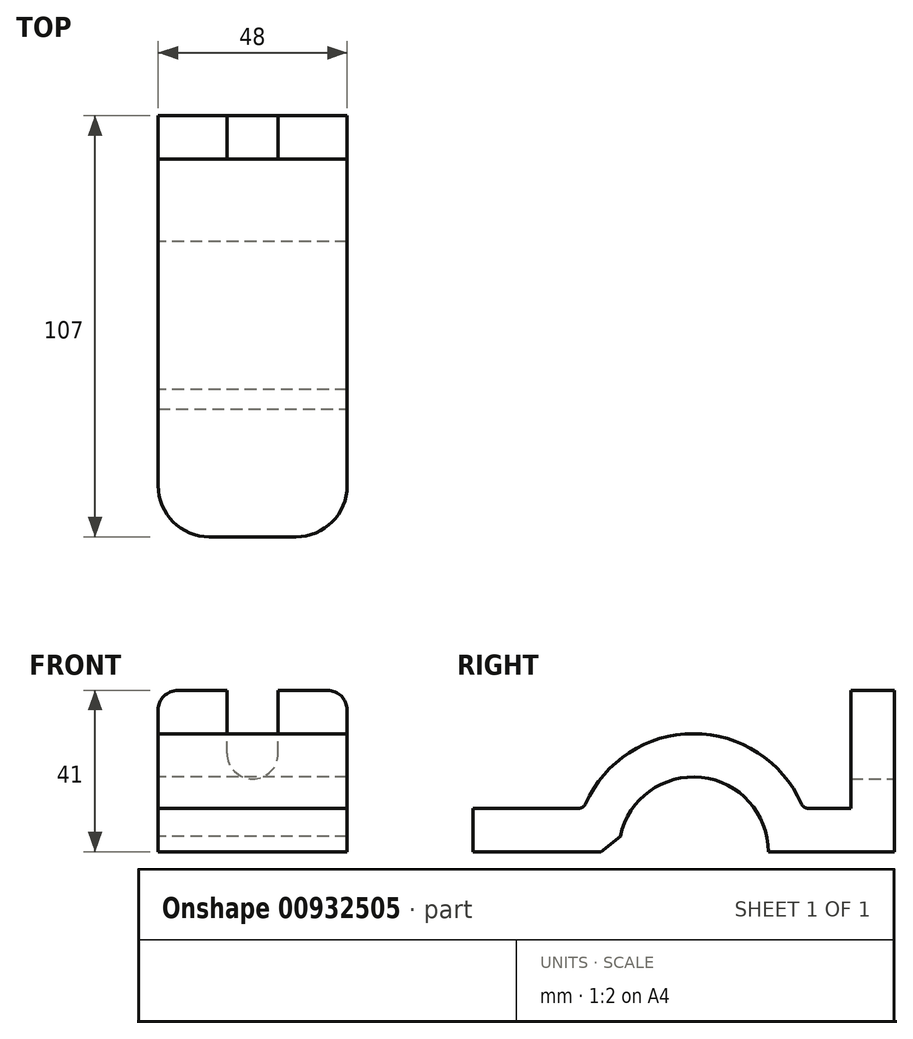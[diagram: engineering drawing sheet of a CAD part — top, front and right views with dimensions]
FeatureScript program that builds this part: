
annotation { "Feature Type Name" : "Feature", "Feature Type Description" : "" }
export const myFeature = defineFeature(function(context is Context, id is Id, definition is map)
    precondition{}
    {
        {
            var Q0;
            Q0=qCreatedBy(makeId("Right.planeOp"),FACE);
            var sketch = newSketch(context, id + "F0", { "sketchPlane" : qUnion([Q0])});
            skCircle(sketch, "E0", {"center": v(0, 0) * mm, "radius": 19 * mm});
            skCircle(sketch, "E1", {"center": v(0, 0) * mm, "radius": 30 * mm});
            skLineSegment(sketch, "E2.bottom", {"start": v(-56, 0) * mm, "end": v(51, 0) * mm});
            skLineSegment(sketch, "E2.top", {"start": v(-56, 11) * mm, "end": v(51, 11) * mm});
            skLineSegment(sketch, "E2.left", {"start": v(-56, 0) * mm, "end": v(-56, 11) * mm});
            skLineSegment(sketch, "E2.right", {"start": v(51, 0) * mm, "end": v(51, 11) * mm});
            skLineSegment(sketch, "E3.bottom", {"start": v(51, 11) * mm, "end": v(40, 11) * mm});
            skLineSegment(sketch, "E3.top", {"start": v(51, 41) * mm, "end": v(40, 41) * mm});
            skLineSegment(sketch, "E3.left", {"start": v(51, 11) * mm, "end": v(51, 41) * mm});
            skLineSegment(sketch, "E3.right", {"start": v(40, 11) * mm, "end": v(40, 41) * mm});
            skSolve(sketch);
        }
        {
            var Q0;
            {var subQ5=sQuery(id+"F0.wireOp",EDGE,"E2.left");Q0=makeQuery(id+"F0.imprint","IMPRINT",FACE,{"disambiguationData":[TD([[makeQuery(id+"F0.imprint","IMPRINT",EDGE,{"derivedFrom":subQ5}),-1.0]])]});}
            var Q1;
            {var subQ0=sQuery(id+"F0.wireOp",EDGE,"E2.bottom");var subQ1=sQuery(id+"F0.wireOp",EDGE,"E0");var subQ2=makeQuery(id+"F0.imprint","INTERSECT",VERTEX,{"disambiguationData":[OD(0.0)],"derivedFrom":[subQ1,subQ0]});Q1=makeQuery(id+"F0.imprint","IMPRINT",FACE,{"disambiguationData":[TD([[makeQuery(id+"F0.imprint","IMPRINT",EDGE,{"disambiguationData":[TD([[subQ2,1.0]])],"derivedFrom":subQ1}),-1.0]])]});}
            var Q2;
            {var subQ0=sQuery(id+"F0.wireOp",EDGE,"E2.top");var subQ1=sQuery(id+"F0.wireOp",EDGE,"E0");var subQ2=makeQuery(id+"F0.imprint","INTERSECT",VERTEX,{"disambiguationData":[OD(0.0)],"derivedFrom":[subQ1,subQ0]});Q2=makeQuery(id+"F0.imprint","IMPRINT",FACE,{"disambiguationData":[TD([[makeQuery(id+"F0.imprint","IMPRINT",EDGE,{"disambiguationData":[TD([[subQ2,1.0]])],"derivedFrom":subQ1}),-1.0]])]});}
            var Q3;
            {var subQ0=sQuery(id+"F0.wireOp",EDGE,"E2.top");var subQ1=sQuery(id+"F0.wireOp",EDGE,"E0");var subQ2=makeQuery(id+"F0.imprint","INTERSECT",VERTEX,{"disambiguationData":[OD(1.0)],"derivedFrom":[subQ1,subQ0]});Q3=makeQuery(id+"F0.imprint","IMPRINT",FACE,{"disambiguationData":[TD([[makeQuery(id+"F0.imprint","IMPRINT",EDGE,{"disambiguationData":[TD([[subQ2,1.0]])],"derivedFrom":subQ1}),-1.0]])]});}
            var Q4;
            {var subQ0=sQuery(id+"F0.wireOp",EDGE,"E2.right");Q4=makeQuery(id+"F0.imprint","IMPRINT",FACE,{"disambiguationData":[TD([[makeQuery(id+"F0.imprint","IMPRINT",EDGE,{"derivedFrom":subQ0}),1.0]])]});}
            var Q5;
            Q5=makeQuery(id+"F0.imprint","IMPRINT",FACE,{"disambiguationData":[TD([[makeQuery(id+"F0.imprint","IMPRINT",EDGE,{"derivedFrom":sQuery(id+"F0.wireOp",EDGE,"E3.top")}),1.0]])]});
            extrude(context, id + "F1", {"entities" : qUnion([Q0, Q1, Q2, Q3, Q4, Q5]), "endBound" : BoundingType.SYMMETRIC, "depth" : 48 * mm});
        }
        {
            var Q0;
            Q0=makeQuery(id+"F1.opExtrude","SWEPT_FACE",FACE,{"disambiguationData":[OSD([sQuery(id+"F0.wireOp",EDGE,"E2.right"),sQuery(id+"F0.wireOp",EDGE,"E3.left")])]});
            var sketch = newSketch(context, id + "F2", { "sketchPlane" : qUnion([Q0])});
            skLineSegment(sketch, "E4", {"start": v(0, 0) * mm, "end": v(0, 41) * mm, "construction": true});
            skCircle(sketch, "E5", {"center": v(0, 25) * mm, "radius": 6.5 * mm});
            skLineSegment(sketch, "E6", {"start": v(-6.5, 25) * mm, "end": v(-6.5, 41) * mm});
            skLineSegment(sketch, "E7", {"start": v(6.5, 25) * mm, "end": v(6.5, 41) * mm});
            skSolve(sketch);
        }
        {
            var Q0;
            {var subQ0=sQuery(id+"F2.wireOp",EDGE,"E5");var subQ2=makeQuery(id+"F2.imprint","INTERSECT",VERTEX,{"derivedFrom":[subQ0,sQuery(id+"F2.wireOp",EDGE,"E6")]});Q0=makeQuery(id+"F2.imprint","IMPRINT",FACE,{"disambiguationData":[TD([[makeQuery(id+"F2.imprint","IMPRINT",EDGE,{"disambiguationData":[TD([[subQ2,1.0]])],"derivedFrom":subQ0}),1.0]])]});}
            var Q1;
            {var subQ2=sQuery(id+"F2.wireOp",EDGE,"E6");Q1=makeQuery(id+"F2.imprint","IMPRINT",FACE,{"disambiguationData":[TD([[makeQuery(id+"F2.imprint","IMPRINT",EDGE,{"derivedFrom":subQ2}),-1.0]])]});}
            var Q2;
            Q2=makeQuery(id+"F1.opExtrude","SWEPT_FACE",FACE,{"disambiguationData":[OSD([sQuery(id+"F0.wireOp",EDGE,"E3.right")])]});
            extrude(context, id + "F3", {"entities" : qUnion([Q0, Q1]), "operationType" : NewBodyOperationType.REMOVE, "endBound" : BoundingType.UP_TO_SURFACE, "oppositeDirection" : true, "endBoundEntityFace" : qUnion([Q2]), "depth" : 25 * mm});
        }
        {
            var Q0;
            Q0=makeQuery(id+"F1.opExtrude","CAP_EDGE",EDGE,{"disambiguationData":[OSD([sQuery(id+"F0.wireOp",EDGE,"E2.left")])],"isStart":false});
            var Q1;
            Q1=makeQuery(id+"F1.opExtrude","CAP_EDGE",EDGE,{"disambiguationData":[OSD([sQuery(id+"F0.wireOp",EDGE,"E2.left")])],"isStart":true});
            fillet(context, id + "F4", {"entities" : qUnion([Q0, Q1]), "radius" : 13 * mm, "tangentPropagation" : true, "allowEdgeOverflow" : false});
        }
        {
            var Q0;
            Q0=makeQuery(id+"F1.opExtrude","CAP_EDGE",EDGE,{"disambiguationData":[OSD([sQuery(id+"F0.wireOp",EDGE,"E3.top")])],"isStart":false});
            var Q1;
            Q1=makeQuery(id+"F1.opExtrude","CAP_EDGE",EDGE,{"disambiguationData":[OSD([sQuery(id+"F0.wireOp",EDGE,"E3.top")])],"isStart":true});
            fillet(context, id + "F5", {"entities" : qUnion([Q0, Q1]), "radius" : 5 * mm, "tangentPropagation" : true, "allowEdgeOverflow" : false});
        }
        {
            var Q0;
            {var subQ0=sQuery(id+"F0.wireOp",EDGE,"E2.top");var subQ1=sQuery(id+"F0.wireOp",EDGE,"E1");Q0=makeQuery(id+"F1.opExtrude","SWEPT_EDGE",EDGE,{"disambiguationData":[OSD([subQ1,subQ0]),TDD([makeQuery(id+"F0.imprint","INTERSECT",VERTEX,{"disambiguationData":[OD(1.0)],"derivedFrom":[subQ1,subQ0]})])]});}
            var Q1;
            {var subQ0=sQuery(id+"F0.wireOp",EDGE,"E2.top");var subQ1=sQuery(id+"F0.wireOp",EDGE,"E1");Q1=makeQuery(id+"F1.opExtrude","SWEPT_EDGE",EDGE,{"disambiguationData":[OSD([subQ1,subQ0]),TDD([makeQuery(id+"F0.imprint","INTERSECT",VERTEX,{"disambiguationData":[OD(0.0)],"derivedFrom":[subQ1,subQ0]})])]});}
            fillet(context, id + "F6", {"entities" : qUnion([Q0, Q1]), "radius" : 2 * mm, "tangentPropagation" : true, "allowEdgeOverflow" : false});
        }
        {
            var Q0;
            {var subQ0=sQuery(id+"F0.wireOp",EDGE,"E2.bottom");var subQ1=sQuery(id+"F0.wireOp",EDGE,"E0");Q0=makeQuery(id+"F1.opExtrude","SWEPT_EDGE",EDGE,{"disambiguationData":[OSD([subQ1,subQ0]),TDD([makeQuery(id+"F0.imprint","INTERSECT",VERTEX,{"disambiguationData":[OD(0.0)],"derivedFrom":[subQ1,subQ0]})])]});}
            chamfer(context, id + "F7", {"entities" : qUnion([Q0]), "width" : 5 * mm, "tangentPropagation" : true});
        }
    });
